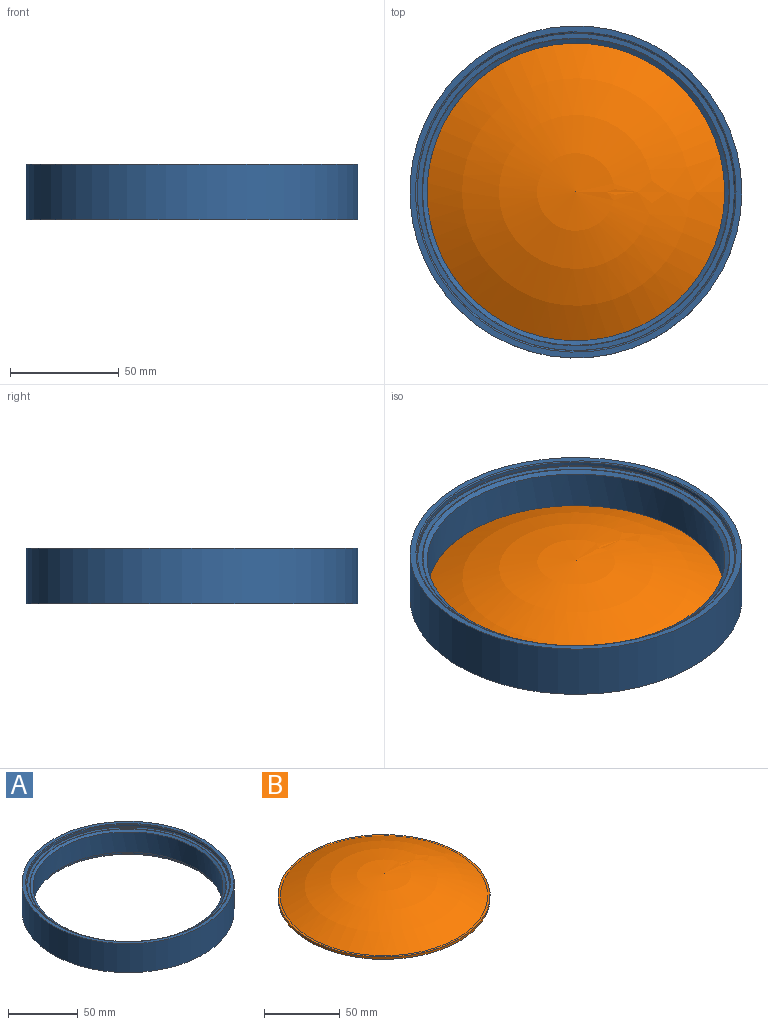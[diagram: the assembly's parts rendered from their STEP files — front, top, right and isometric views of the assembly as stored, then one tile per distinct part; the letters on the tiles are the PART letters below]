
ASSEMBLY  parts=2 mates=1
PART A: 13 faces, bbox 159.2x159.2x25.4 mm
  f0: cylinder r=76.2mm len=152.4mm, axis (0,0,-1), area 12161mm2, adj f1,f2
  f1: plane 152.4x152.4mm, normal (0,0,1), area 1254.6mm2, adj f0,f6
  f2: plane 152.4x152.4mm, normal (0,0,-1), area 2351.1mm2, adj f0,f12
  f3: plane 145.54x145.54mm, normal (0,0,1), area 969.4mm2, adj f5,f8
  f4: cylinder r=73.03mm len=146.05mm, axis (0,0,1), area 815.8mm2, adj f5,f6
  f5: torus R=72.77mm, axis (0,0,1), area 182.8mm2, adj f3,f4
  f6: torus R=73.53mm, axis (0,0,1), area 367.1mm2, adj f1,f4
  f7: cone r=70.48mm half-angle=60.5deg, axis (0,0,1), area 1022.9mm2, adj f8,f11
  f8: torus R=70.62mm, axis (0,0,1), area 116mm2, adj f3,f7
  f9: plane 139.7x139.7mm, normal (0,0,-1), area 661.6mm2, adj f10,f11
  f10: cylinder r=69.85mm len=139.7mm, axis (0,0,-1), area 1114.8mm2, adj f9,f12
  f11: cylinder r=68.33mm len=136.65mm, axis (0,0,-1), area 7653mm2, adj f7,f9
  f12: cone r=69.85mm half-angle=45deg, axis (0,0,-1), area 795.4mm2, adj f2,f10
PART B: 5 faces, bbox 139.7x139.7x19.8 mm
  f0: sphere r=139.7mm, area 10922mm2, adj f1
  f1: plane 139.7x139.7mm, normal (0,0,-1), area 4892.3mm2, adj f0,f2
  f2: cylinder r=69.85mm len=139.7mm, axis (0,0,1), area 836.1mm2, adj f1,f3
  f3: plane 139.7x139.7mm, normal (0,0,1), area 661.6mm2, adj f2,f4
  f4: sphere r=139.7mm, area 15667.2mm2, adj f3
PLACE A t=(-15.32,9.61,14.99)mm
PLACE B t=(-15.32,9.61,16.9)mm
MATE fastened B.f2 <-> A.f10  axis (0,0,1) through (-15.32,9.61,18.8)mm
